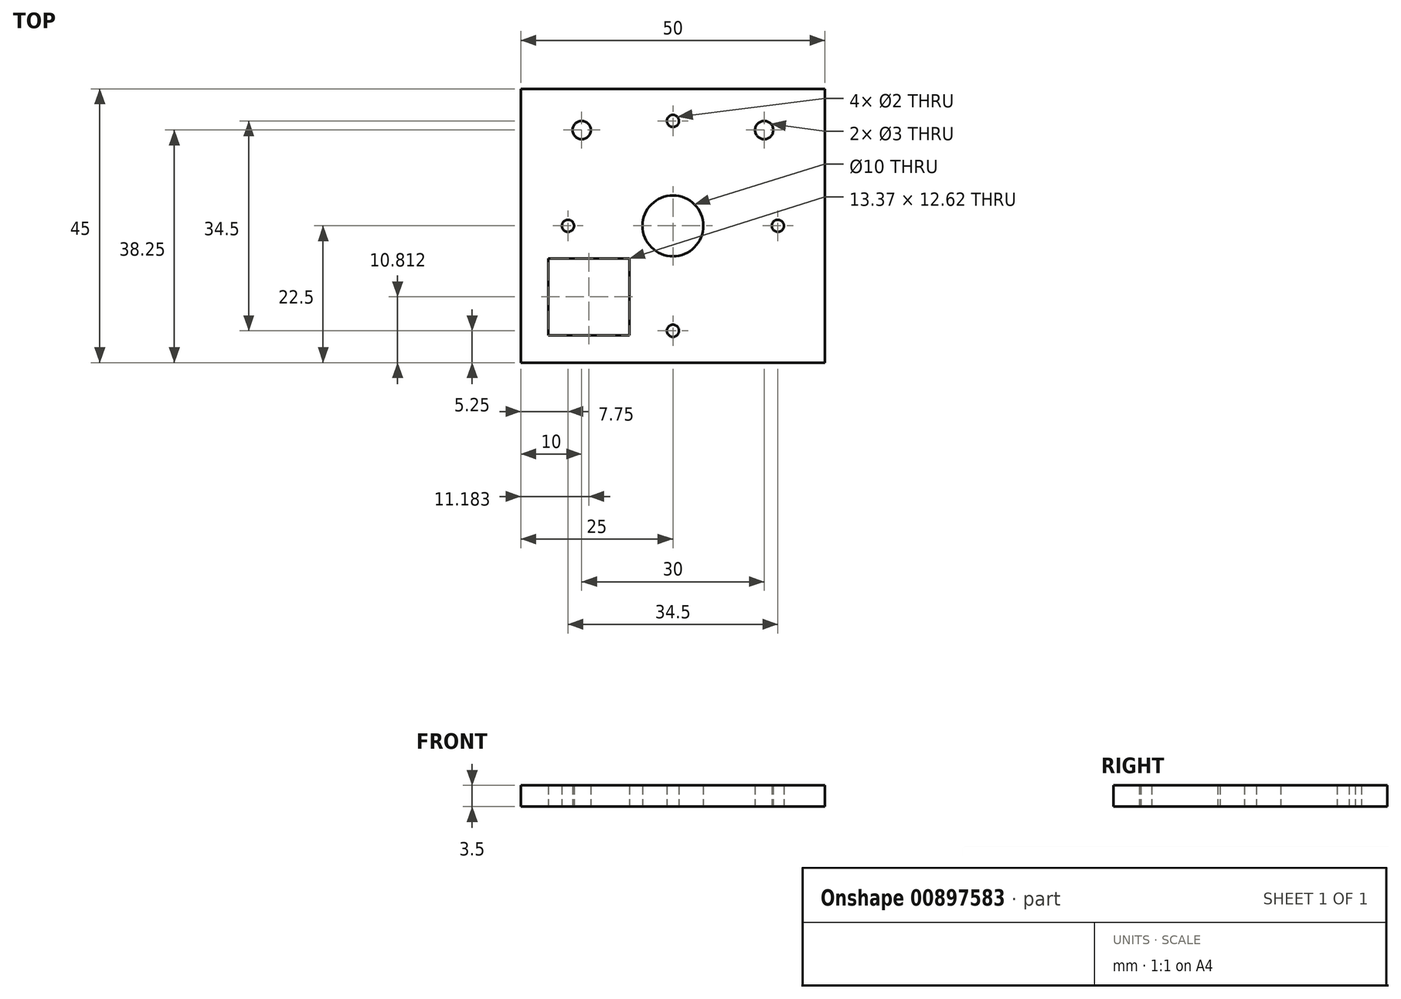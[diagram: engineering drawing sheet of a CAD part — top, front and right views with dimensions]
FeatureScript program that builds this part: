
annotation { "Feature Type Name" : "Feature", "Feature Type Description" : "" }
export const myFeature = defineFeature(function(context is Context, id is Id, definition is map)
    precondition{}
    {
        {
            var Q0;
            Q0=qCreatedBy(makeId("Top.planeOp"),FACE);
            var sketch = newSketch(context, id + "F0", { "sketchPlane" : qUnion([Q0])});
            skLineSegment(sketch, "E0.bottom", {"start": v(25, 22.5) * mm, "end": v(-25, 22.5) * mm});
            skLineSegment(sketch, "E0.top", {"start": v(25, -22.5) * mm, "end": v(-25, -22.5) * mm});
            skLineSegment(sketch, "E0.left", {"start": v(25, 22.5) * mm, "end": v(25, -22.5) * mm});
            skLineSegment(sketch, "E0.right", {"start": v(-25, 22.5) * mm, "end": v(-25, -22.5) * mm});
            skPoint(sketch, "E0.middle", {"position": v(0, 0) * mm});
            skCircle(sketch, "E1", {"center": v(0, 0) * mm, "radius": 5 * mm});
            skCircle(sketch, "E2", {"center": v(0, 0) * mm, "radius": 17.25 * mm, "construction": true});
            skLineSegment(sketch, "E3", {"start": v(-25, 0) * mm, "end": v(35.79, 0) * mm, "construction": true});
            skPoint(sketch, "E3.endSnap0", {"position": v(25, 0) * mm});
            skLineSegment(sketch, "E4", {"start": v(0, -22.5) * mm, "end": v(0, 36.35) * mm, "construction": true});
            skCircle(sketch, "E5", {"center": v(0, 17.25) * mm, "radius": 1 * mm});
            skCircle(sketch, "E6", {"center": v(17.25, 0) * mm, "radius": 1 * mm});
            skCircle(sketch, "E7", {"center": v(0, -17.25) * mm, "radius": 1 * mm});
            skCircle(sketch, "E8", {"center": v(-17.25, 0) * mm, "radius": 1 * mm});
            skLineSegment(sketch, "E9.bottom", {"start": v(-25, -22.5) * mm, "end": v(-5, -22.5) * mm, "construction": true});
            skLineSegment(sketch, "E9.top", {"start": v(-25, -18) * mm, "end": v(-5, -18) * mm, "construction": true});
            skLineSegment(sketch, "E9.left", {"start": v(-25, -22.5) * mm, "end": v(-25, -18) * mm, "construction": true});
            skLineSegment(sketch, "E9.right", {"start": v(-5, -22.5) * mm, "end": v(-5, -18) * mm, "construction": true});
            skLineSegment(sketch, "E10.bottom", {"start": v(-25, -22.5) * mm, "end": v(-20.5, -22.5) * mm, "construction": true});
            skLineSegment(sketch, "E10.top", {"start": v(-25, -2.5) * mm, "end": v(-20.5, -2.5) * mm, "construction": true});
            skLineSegment(sketch, "E10.left", {"start": v(-25, -22.5) * mm, "end": v(-25, -2.5) * mm, "construction": true});
            skLineSegment(sketch, "E10.right", {"start": v(-20.5, -22.5) * mm, "end": v(-20.5, -2.5) * mm, "construction": true});
            skLineSegment(sketch, "E11.bottom", {"start": v(-20.5, -18) * mm, "end": v(-7.13, -18) * mm});
            skLineSegment(sketch, "E11.top", {"start": v(-20.5, -5.38) * mm, "end": v(-7.13, -5.38) * mm});
            skLineSegment(sketch, "E11.left", {"start": v(-20.5, -18) * mm, "end": v(-20.5, -5.38) * mm});
            skLineSegment(sketch, "E11.right", {"start": v(-7.13, -18) * mm, "end": v(-7.13, -5.38) * mm});
            skLineSegment(sketch, "E12", {"start": v(25, -22.5) * mm, "end": v(34.22, -22.5) * mm, "construction": true});
            skLineSegment(sketch, "E13", {"start": v(34.22, -22.5) * mm, "end": v(34.22, 13.5) * mm, "construction": true});
            skLineSegment(sketch, "E14", {"start": v(34.22, 13.5) * mm, "end": v(-31.92, 13.5) * mm, "construction": true});
            skLineSegment(sketch, "E15", {"start": v(-31.92, 13.5) * mm, "end": v(-31.92, 18) * mm, "construction": true});
            skLineSegment(sketch, "E16", {"start": v(-31.92, 18) * mm, "end": v(34.22, 18) * mm, "construction": true});
            skLineSegment(sketch, "E17", {"start": v(-31.92, 15.75) * mm, "end": v(34.5, 15.75) * mm, "construction": true});
            skCircle(sketch, "E18", {"center": v(0, 15.75) * mm, "radius": 15 * mm, "construction": true});
            skCircle(sketch, "E19", {"center": v(-15, 15.75) * mm, "radius": 1.5 * mm});
            skCircle(sketch, "E20", {"center": v(15, 15.75) * mm, "radius": 1.5 * mm});
            skSolve(sketch);
        }
        {
            var Q0;
            Q0=makeQuery(id+"F0.imprint","IMPRINT",FACE,{"disambiguationData":[TD([[makeQuery(id+"F0.imprint","IMPRINT",EDGE,{"derivedFrom":sQuery(id+"F0.wireOp",EDGE,"E0.bottom")}),1.0]])]});
            extrude(context, id + "F1", {"entities" : qUnion([Q0]), "depth" : 3.5 * mm, "offsetDistance" : 25 * mm});
        }
    });
